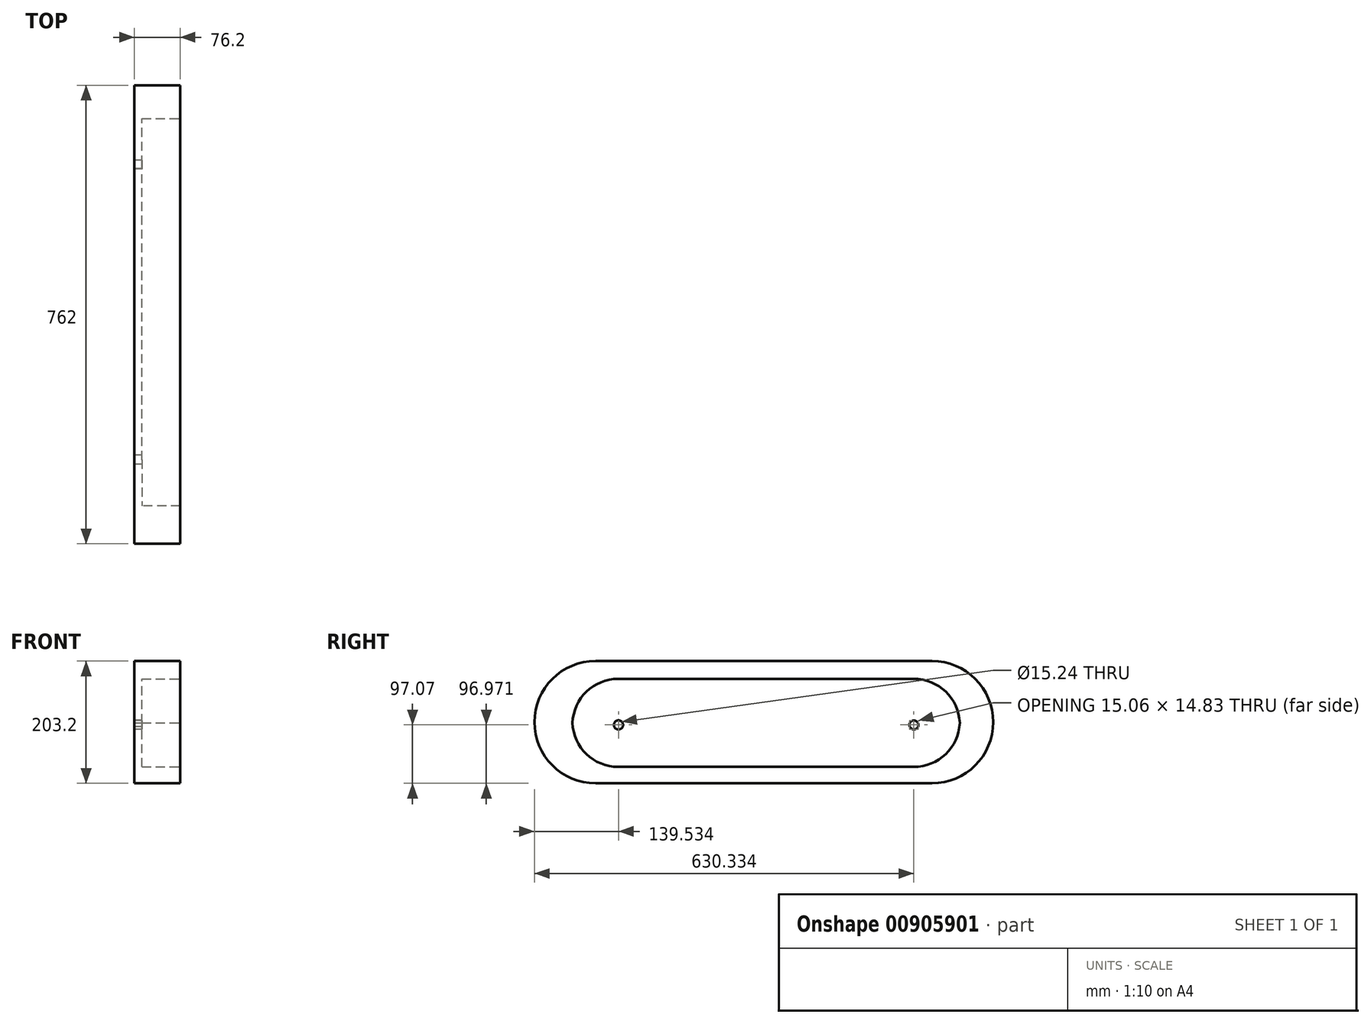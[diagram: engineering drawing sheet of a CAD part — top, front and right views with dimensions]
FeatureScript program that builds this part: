
annotation { "Feature Type Name" : "Feature", "Feature Type Description" : "" }
export const myFeature = defineFeature(function(context is Context, id is Id, definition is map)
    precondition{}
    {
        {
            var Q0;
            Q0=qCreatedBy(makeId("Right.planeOp"),FACE);
            var sketch = newSketch(context, id + "F0", { "sketchPlane" : qUnion([Q0])});
            skLineSegment(sketch, "E0.bottom", {"start": v(-360.72, 87.78) * mm, "end": v(401.28, 87.78) * mm});
            skLineSegment(sketch, "E0.top", {"start": v(-360.72, -115.42) * mm, "end": v(401.28, -115.42) * mm});
            skLineSegment(sketch, "E0.left", {"start": v(-360.72, 87.78) * mm, "end": v(-360.72, -115.42) * mm});
            skLineSegment(sketch, "E0.right", {"start": v(401.28, 87.78) * mm, "end": v(401.28, -115.42) * mm});
            skSolve(sketch);
        }
        {
            var Q0;
            Q0=makeQuery(id+"F0.imprint","IMPRINT",FACE,{"disambiguationData":[TD([[makeQuery(id+"F0.imprint","IMPRINT",EDGE,{"derivedFrom":sQuery(id+"F0.wireOp",EDGE,"E0.bottom")}),-1.0]])]});
            extrude(context, id + "F1", {"entities" : qUnion([Q0]), "depth" : 76.2 * mm, "offsetDistance" : 25.4 * mm});
        }
        {
            var Q0;
            Q0=makeQuery(id+"F1.opExtrude","SWEPT_EDGE",EDGE,{"disambiguationData":[OSD([sQuery(id+"F0.wireOp",EDGE,"E0.bottom"),sQuery(id+"F0.wireOp",EDGE,"E0.left")])]});
            var Q1;
            Q1=makeQuery(id+"F1.opExtrude","SWEPT_EDGE",EDGE,{"disambiguationData":[OSD([sQuery(id+"F0.wireOp",EDGE,"E0.top"),sQuery(id+"F0.wireOp",EDGE,"E0.left")])]});
            var Q2;
            Q2=makeQuery(id+"F1.opExtrude","SWEPT_EDGE",EDGE,{"disambiguationData":[OSD([sQuery(id+"F0.wireOp",EDGE,"E0.bottom"),sQuery(id+"F0.wireOp",EDGE,"E0.right")])]});
            var Q3;
            Q3=makeQuery(id+"F1.opExtrude","SWEPT_EDGE",EDGE,{"disambiguationData":[OSD([sQuery(id+"F0.wireOp",EDGE,"E0.top"),sQuery(id+"F0.wireOp",EDGE,"E0.right")])]});
            fillet(context, id + "F2", {"entities" : qUnion([Q0, Q1, Q2, Q3]), "radius" : 101.6 * mm, "tangentPropagation" : true, "allowEdgeOverflow" : false});
        }
        {
            var Q0;
            Q0=makeQuery(id+"F1.opExtrude","CAP_FACE",FACE,{"disambiguationData":[OSD([sQuery(id+"F0.wireOp",EDGE,"E0.bottom"),sQuery(id+"F0.wireOp",EDGE,"E0.top"),sQuery(id+"F0.wireOp",EDGE,"E0.left"),sQuery(id+"F0.wireOp",EDGE,"E0.right")])],"isStart":false});
            var sketch = newSketch(context, id + "F3", { "sketchPlane" : qUnion([Q0])});
            skLineSegment(sketch, "E1.bottom", {"start": v(-297.63, 58.1) * mm, "end": v(345.86, 58.1) * mm});
            skLineSegment(sketch, "E1.top", {"start": v(-297.63, -88.3) * mm, "end": v(345.86, -88.3) * mm});
            skLineSegment(sketch, "E1.left", {"start": v(-297.63, 58.1) * mm, "end": v(-297.63, -88.3) * mm});
            skLineSegment(sketch, "E1.right", {"start": v(345.86, 58.1) * mm, "end": v(345.86, -88.3) * mm});
            skSolve(sketch);
        }
        {
            var Q0;
            Q0 = qSketchRegion(id + "F3", true);
            extrude(context, id + "F4", {"entities" : qUnion([Q0]), "operationType" : NewBodyOperationType.REMOVE, "oppositeDirection" : true, "depth" : 63.5 * mm, "offsetDistance" : 25.4 * mm});
        }
        {
            var Q0;
            Q0=makeQuery(id+"F4.boolean.opBoolean","COPY",EDGE,{"derivedFrom":makeQuery(id+"F4.opExtrude","SWEPT_EDGE",EDGE,{"disambiguationData":[OSD([sQuery(id+"F3.wireOp",EDGE,"E1.bottom"),sQuery(id+"F3.wireOp",EDGE,"E1.left")])]})});
            var Q1;
            Q1=makeQuery(id+"F4.boolean.opBoolean","COPY",EDGE,{"derivedFrom":makeQuery(id+"F4.opExtrude","SWEPT_EDGE",EDGE,{"disambiguationData":[OSD([sQuery(id+"F3.wireOp",EDGE,"E1.top"),sQuery(id+"F3.wireOp",EDGE,"E1.left")])]})});
            var Q2;
            Q2=makeQuery(id+"F4.boolean.opBoolean","COPY",EDGE,{"derivedFrom":makeQuery(id+"F4.opExtrude","SWEPT_EDGE",EDGE,{"disambiguationData":[OSD([sQuery(id+"F3.wireOp",EDGE,"E1.bottom"),sQuery(id+"F3.wireOp",EDGE,"E1.right")])]})});
            var Q3;
            Q3=makeQuery(id+"F4.boolean.opBoolean","COPY",EDGE,{"derivedFrom":makeQuery(id+"F4.opExtrude","SWEPT_EDGE",EDGE,{"disambiguationData":[OSD([sQuery(id+"F3.wireOp",EDGE,"E1.top"),sQuery(id+"F3.wireOp",EDGE,"E1.right")])]})});
            fillet(context, id + "F5", {"entities" : qUnion([Q0, Q1, Q2, Q3]), "radius" : 76.2 * mm, "tangentPropagation" : true, "allowEdgeOverflow" : false});
        }
        {
            var Q0;
            Q0=makeQuery(id+"F1.opExtrude","CAP_FACE",FACE,{"disambiguationData":[OSD([sQuery(id+"F0.wireOp",EDGE,"E0.bottom"),sQuery(id+"F0.wireOp",EDGE,"E0.top"),sQuery(id+"F0.wireOp",EDGE,"E0.left"),sQuery(id+"F0.wireOp",EDGE,"E0.right")])],"isStart":true});
            var sketch = newSketch(context, id + "F6", { "sketchPlane" : qUnion([Q0])});
            skCircle(sketch, "E2", {"center": v(-269.53, -18.65) * mm, "radius": 7.62 * mm});
            skSolve(sketch);
        }
        {
            var Q0;
            Q0=makeQuery(id+"F6.imprint","IMPRINT",FACE,{"disambiguationData":[TD([[makeQuery(id+"F6.imprint","IMPRINT",EDGE,{"derivedFrom":sQuery(id+"F6.wireOp",EDGE,"E2")}),-1.0]])]});
            var sketch = newSketch(context, id + "F7", { "sketchPlane" : qUnion([Q0])});
            skCircle(sketch, "E3", {"center": v(-269.7, -18.25) * mm, "radius": 7.62 * mm});
            skSolve(sketch);
        }
        {
            var Q0;
            {var subQ0=sQuery(id+"F7.wireOp",EDGE,"E3");var subQ1=makeQuery(id+"F6.imprint","IMPRINT",EDGE,{"derivedFrom":sQuery(id+"F6.wireOp",EDGE,"E2")});var subQ2=makeQuery(id+"F7.imprint","INTERSECT",VERTEX,{"disambiguationData":[OD(0.0)],"derivedFrom":[subQ1,subQ0]});Q0=makeQuery(id+"F7.imprint","IMPRINT",FACE,{"disambiguationData":[TD([[makeQuery(id+"F7.imprint","IMPRINT",EDGE,{"disambiguationData":[TD([[subQ2,1.0]])],"derivedFrom":subQ0}),1.0]])]});}
            extrude(context, id + "F8", {"entities" : qUnion([Q0]), "operationType" : NewBodyOperationType.REMOVE, "oppositeDirection" : true, "depth" : 25.4 * mm, "offsetDistance" : 25.4 * mm});
        }
        {
            var Q0;
            Q0=makeQuery(id+"F6.imprint","IMPRINT",FACE,{"disambiguationData":[TD([[makeQuery(id+"F6.imprint","IMPRINT",EDGE,{"derivedFrom":sQuery(id+"F6.wireOp",EDGE,"E2")}),-1.0]])]});
            var sketch = newSketch(context, id + "F9", { "sketchPlane" : qUnion([Q0])});
            skCircle(sketch, "E4", {"center": v(221.19, -18.35) * mm, "radius": 7.62 * mm});
            skSolve(sketch);
        }
        {
            var Q0;
            Q0=makeQuery(id+"F9.imprint","IMPRINT",FACE,{"disambiguationData":[TD([[makeQuery(id+"F9.imprint","IMPRINT",EDGE,{"derivedFrom":sQuery(id+"F9.wireOp",EDGE,"E4")}),1.0]])]});
            extrude(context, id + "F10", {"entities" : qUnion([Q0]), "operationType" : NewBodyOperationType.REMOVE, "oppositeDirection" : true, "depth" : 25.4 * mm, "offsetDistance" : 25.4 * mm});
        }
    });
